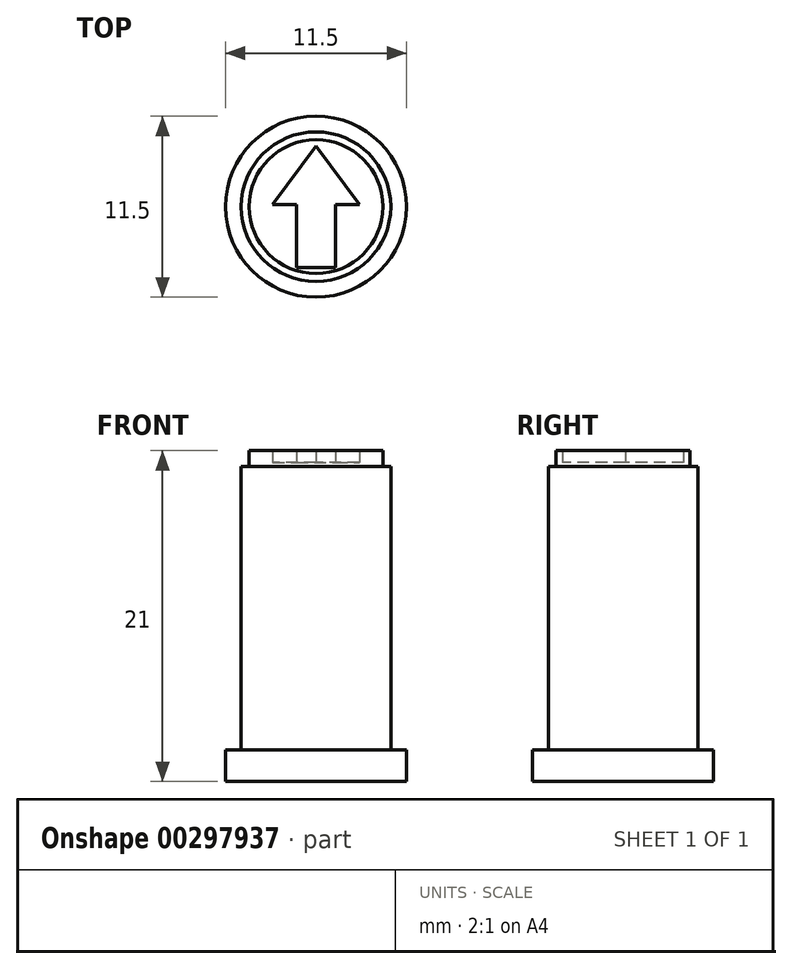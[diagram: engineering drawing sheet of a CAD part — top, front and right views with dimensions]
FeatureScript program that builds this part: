
annotation { "Feature Type Name" : "Feature", "Feature Type Description" : "" }
export const myFeature = defineFeature(function(context is Context, id is Id, definition is map)
    precondition{}
    {
        {
            var Q0;
            Q0=qCreatedBy(makeId("Top.planeOp"),FACE);
            var sketch = newSketch(context, id + "F0", { "sketchPlane" : qUnion([Q0])});
            skArc(sketch, "E0", {"start": v(0, 4.75) * mm, "mid": v(-3.36, 3.36) * mm, "end": v(-4.75, 0) * mm});
            skArc(sketch, "E1", {"start": v(-4.75, 0) * mm, "mid": v(-3.36, -3.36) * mm, "end": v(0, -4.75) * mm});
            skArc(sketch, "E2", {"start": v(0, -4.75) * mm, "mid": v(3.36, -3.36) * mm, "end": v(4.75, 0) * mm});
            skArc(sketch, "E3", {"start": v(4.75, 0) * mm, "mid": v(3.36, 3.36) * mm, "end": v(0, 4.75) * mm});
            skArc(sketch, "E4", {"start": v(0, -5.75) * mm, "mid": v(4.07, -4.07) * mm, "end": v(5.75, 0) * mm});
            skArc(sketch, "E5", {"start": v(5.75, 0) * mm, "mid": v(4.07, 4.07) * mm, "end": v(0, 5.75) * mm});
            skArc(sketch, "E6", {"start": v(0, 5.75) * mm, "mid": v(-4.07, 4.07) * mm, "end": v(-5.75, 0) * mm});
            skArc(sketch, "E7", {"start": v(-5.75, 0) * mm, "mid": v(-4.07, -4.07) * mm, "end": v(0, -5.75) * mm});
            skArc(sketch, "E8", {"start": v(-4.25, 0) * mm, "mid": v(-3, -3) * mm, "end": v(0, -4.25) * mm});
            skArc(sketch, "E9", {"start": v(0, -4.25) * mm, "mid": v(3, -3) * mm, "end": v(4.25, 0) * mm});
            skArc(sketch, "E10", {"start": v(4.25, 0) * mm, "mid": v(3, 3) * mm, "end": v(0, 4.25) * mm});
            skArc(sketch, "E11", {"start": v(0, 4.25) * mm, "mid": v(-3, 3) * mm, "end": v(-4.25, 0) * mm});
            skLineSegment(sketch, "E12", {"start": v(-1.25, -3.85) * mm, "end": v(1.25, -3.85) * mm});
            skLineSegment(sketch, "E13", {"start": v(1.25, -3.85) * mm, "end": v(1.25, 0.15) * mm});
            skLineSegment(sketch, "E14", {"start": v(1.25, 0.15) * mm, "end": v(2.75, 0.15) * mm});
            skLineSegment(sketch, "E15", {"start": v(2.75, 0.15) * mm, "end": v(0, 3.85) * mm});
            skLineSegment(sketch, "E16", {"start": v(0, 3.85) * mm, "end": v(-2.75, 0.15) * mm});
            skLineSegment(sketch, "E17", {"start": v(-2.75, 0.15) * mm, "end": v(-1.25, 0.15) * mm});
            skLineSegment(sketch, "E18", {"start": v(-1.25, 0.15) * mm, "end": v(-1.25, -3.85) * mm});
            skSolve(sketch);
        }
        {
            var Q0;
            Q0=makeQuery(id+"F0.imprint","IMPRINT",FACE,{"disambiguationData":[TD([[makeQuery(id+"F0.imprint","IMPRINT",EDGE,{"derivedFrom":sQuery(id+"F0.wireOp",EDGE,"E8")}),1.0]])]});
            extrude(context, id + "F1", {"entities" : qUnion([Q0]), "depth" : 21 * mm});
        }
        {
            var Q0;
            Q0=makeQuery(id+"F0.imprint","IMPRINT",FACE,{"disambiguationData":[TD([[makeQuery(id+"F0.imprint","IMPRINT",EDGE,{"derivedFrom":sQuery(id+"F0.wireOp",EDGE,"E0")}),1.0]])]});
            extrude(context, id + "F2", {"entities" : qUnion([Q0]), "operationType" : NewBodyOperationType.ADD, "depth" : 20 * mm});
        }
        {
            var Q0;
            Q0=makeQuery(id+"F0.imprint","IMPRINT",FACE,{"disambiguationData":[TD([[makeQuery(id+"F0.imprint","IMPRINT",EDGE,{"derivedFrom":sQuery(id+"F0.wireOp",EDGE,"E0")}),-1.0]])]});
            extrude(context, id + "F3", {"entities" : qUnion([Q0]), "operationType" : NewBodyOperationType.ADD, "depth" : 2 * mm});
        }
        {
            var Q0;
            Q0=makeQuery(id+"F0.imprint","IMPRINT",FACE,{"disambiguationData":[TD([[makeQuery(id+"F0.imprint","IMPRINT",EDGE,{"derivedFrom":sQuery(id+"F0.wireOp",EDGE,"E12")}),1.0]])]});
            extrude(context, id + "F4", {"entities" : qUnion([Q0]), "operationType" : NewBodyOperationType.ADD, "depth" : 20.25 * mm});
        }
    });
